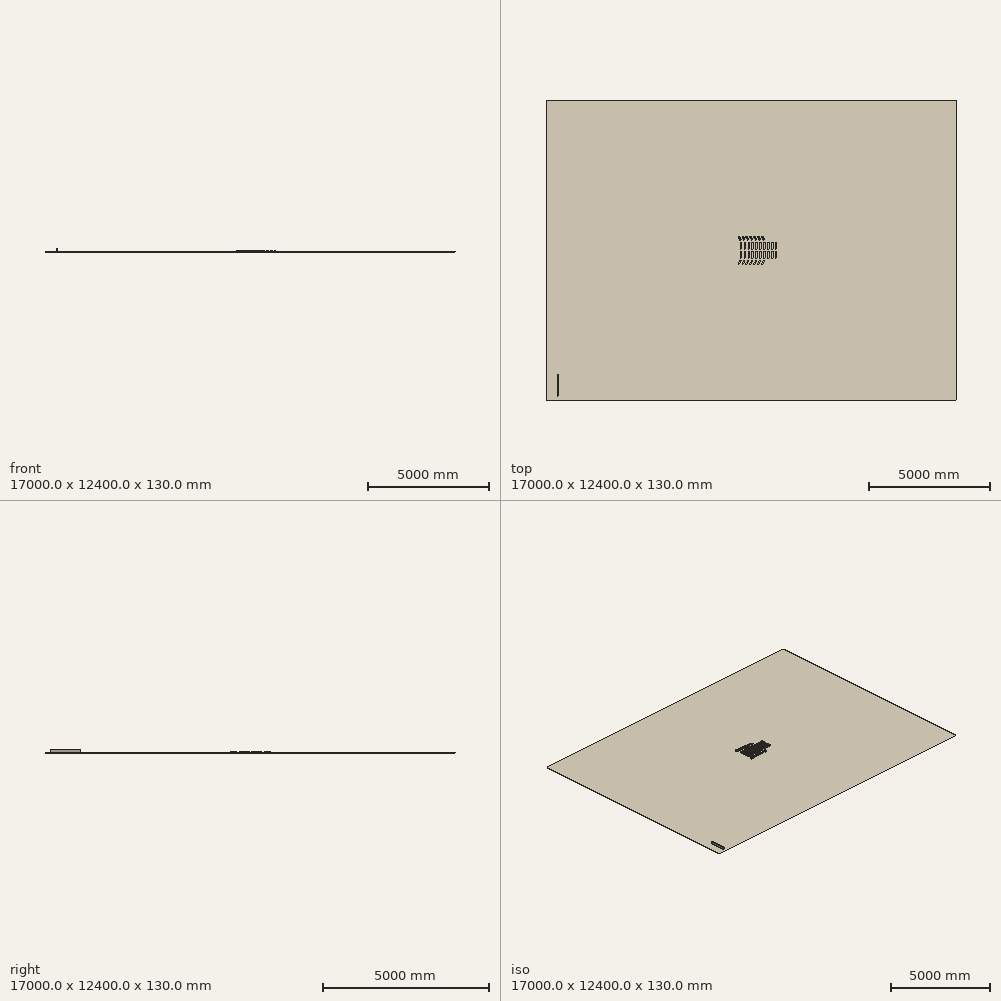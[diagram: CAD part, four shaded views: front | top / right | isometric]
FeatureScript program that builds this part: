
annotation { "Feature Type Name" : "Feature", "Feature Type Description" : "" }
export const myFeature = defineFeature(function(context is Context, id is Id, definition is map)
    precondition{}
    {
        {
            var Q0;
            Q0=qCreatedBy(makeId("Top.planeOp"),FACE);
            var sketch = newSketch(context, id + "F0", { "sketchPlane" : qUnion([Q0])});
            skLineSegment(sketch, "E0.bottom", {"start": v(8500, -6200) * mm, "end": v(-8500, -6200) * mm});
            skLineSegment(sketch, "E0.top", {"start": v(8500, 6200) * mm, "end": v(-8500, 6200) * mm});
            skLineSegment(sketch, "E0.left", {"start": v(8500, -6200) * mm, "end": v(8500, 6200) * mm});
            skLineSegment(sketch, "E0.right", {"start": v(-8500, -6200) * mm, "end": v(-8500, 6200) * mm});
            skPoint(sketch, "E0.middle", {"position": v(0, 0) * mm});
            skSolve(sketch);
        }
        {
            var Q0;
            Q0 = qSketchRegion(id + "F0", true);
            extrude(context, id + "F1", {"entities" : qUnion([Q0]), "depth" : 20 * mm});
        }
        {
            var Q0;
            Q0=qCreatedBy(makeId("Top.planeOp"),FACE);
            var sketch = newSketch(context, id + "F2", { "sketchPlane" : qUnion([Q0])});
            skLineSegment(sketch, "E1.bottom", {"start": v(-8040, -5150) * mm, "end": v(-8000, -5150) * mm});
            skLineSegment(sketch, "E1.top", {"start": v(-8040, -6050) * mm, "end": v(-8000, -6050) * mm});
            skLineSegment(sketch, "E1.left", {"start": v(-8040, -5150) * mm, "end": v(-8040, -6050) * mm});
            skLineSegment(sketch, "E1.right", {"start": v(-8000, -5150) * mm, "end": v(-8000, -6050) * mm});
            skSolve(sketch);
        }
        {
            var Q0;
            Q0 = qSketchRegion(id + "F2", true);
            extrude(context, id + "F3", {"entities" : qUnion([Q0]), "depth" : 130 * mm});
        }
        {
            var Q0;
            Q0=makeQuery(id+"F1.opExtrude","CAP_FACE",FACE,{"disambiguationData":[OSD([sQuery(id+"F0.wireOp",EDGE,"E0.bottom"),sQuery(id+"F0.wireOp",EDGE,"E0.top"),sQuery(id+"F0.wireOp",EDGE,"E0.left"),sQuery(id+"F0.wireOp",EDGE,"E0.right")])],"isStart":false});
            var sketch = newSketch(context, id + "F4", { "sketchPlane" : qUnion([Q0])});
            skLineSegment(sketch, "E2", {"start": v(-518.43, 595) * mm, "end": v(-428.43, 439.12) * mm});
            skLineSegment(sketch, "E3.0", {"start": v(-561.73, 570) * mm, "end": v(-471.73, 414.12) * mm});
            skLineSegment(sketch, "E4", {"start": v(-561.73, 570) * mm, "end": v(-518.43, 595) * mm});
            skLineSegment(sketch, "E5", {"start": v(-471.73, 414.12) * mm, "end": v(-428.43, 439.12) * mm});
            skLineSegment(sketch, "E6.1.0.0", {"start": v(-398.41, 570) * mm, "end": v(-308.41, 414.12) * mm});
            skLineSegment(sketch, "E6.1.0.1", {"start": v(-308.41, 414.12) * mm, "end": v(-265.11, 439.12) * mm});
            skLineSegment(sketch, "E6.1.0.2", {"start": v(-355.11, 595) * mm, "end": v(-265.11, 439.12) * mm});
            skLineSegment(sketch, "E6.1.0.3", {"start": v(-398.41, 570) * mm, "end": v(-355.11, 595) * mm});
            skLineSegment(sketch, "E6.2.0.0", {"start": v(-235.1, 570) * mm, "end": v(-145.1, 414.12) * mm});
            skLineSegment(sketch, "E6.2.0.1", {"start": v(-145.1, 414.12) * mm, "end": v(-101.8, 439.12) * mm});
            skLineSegment(sketch, "E6.2.0.2", {"start": v(-191.8, 595) * mm, "end": v(-101.8, 439.12) * mm});
            skLineSegment(sketch, "E6.2.0.3", {"start": v(-235.1, 570) * mm, "end": v(-191.8, 595) * mm});
            skLineSegment(sketch, "E6.3.0.0", {"start": v(-71.78, 570) * mm, "end": v(18.22, 414.12) * mm});
            skLineSegment(sketch, "E6.3.0.1", {"start": v(18.22, 414.12) * mm, "end": v(61.53, 439.12) * mm});
            skLineSegment(sketch, "E6.3.0.2", {"start": v(-28.47, 595) * mm, "end": v(61.53, 439.12) * mm});
            skLineSegment(sketch, "E6.3.0.3", {"start": v(-71.78, 570) * mm, "end": v(-28.47, 595) * mm});
            skLineSegment(sketch, "E6.4.0.0", {"start": v(91.54, 570) * mm, "end": v(181.54, 414.12) * mm});
            skLineSegment(sketch, "E6.4.0.1", {"start": v(181.54, 414.12) * mm, "end": v(224.85, 439.12) * mm});
            skLineSegment(sketch, "E6.4.0.2", {"start": v(134.85, 595) * mm, "end": v(224.85, 439.12) * mm});
            skLineSegment(sketch, "E6.4.0.3", {"start": v(91.54, 570) * mm, "end": v(134.85, 595) * mm});
            skLineSegment(sketch, "E6.5.0.0", {"start": v(254.86, 570) * mm, "end": v(344.86, 414.12) * mm});
            skLineSegment(sketch, "E6.5.0.1", {"start": v(344.86, 414.12) * mm, "end": v(388.16, 439.12) * mm});
            skLineSegment(sketch, "E6.5.0.2", {"start": v(298.16, 595) * mm, "end": v(388.16, 439.12) * mm});
            skLineSegment(sketch, "E6.5.0.3", {"start": v(254.86, 570) * mm, "end": v(298.16, 595) * mm});
            skLineSegment(sketch, "E6.6.0.0", {"start": v(418.18, 570) * mm, "end": v(508.18, 414.12) * mm});
            skLineSegment(sketch, "E6.6.0.1", {"start": v(508.18, 414.12) * mm, "end": v(551.48, 439.12) * mm});
            skLineSegment(sketch, "E6.6.0.2", {"start": v(461.48, 595) * mm, "end": v(551.48, 439.12) * mm});
            skLineSegment(sketch, "E6.6.0.3", {"start": v(418.18, 570) * mm, "end": v(461.48, 595) * mm});
            skLineSegment(sketch, "E6.direction1", {"start": v(-561.73, 570) * mm, "end": v(-398.41, 570) * mm, "construction": true});
            skLineSegment(sketch, "E7", {"start": v(-8500, 0) * mm, "end": v(8500, 0) * mm, "construction": true});
            skLineSegment(sketch, "E8.bottom", {"start": v(-469.55, 30) * mm, "end": v(-409.55, 30) * mm});
            skLineSegment(sketch, "E8.top", {"start": v(-469.55, 328.32) * mm, "end": v(-409.55, 328.32) * mm});
            skLineSegment(sketch, "E8.left", {"start": v(-469.55, 30) * mm, "end": v(-469.55, 328.32) * mm});
            skLineSegment(sketch, "E8.right", {"start": v(-409.55, 30) * mm, "end": v(-409.55, 328.32) * mm});
            skLineSegment(sketch, "E9.1.0.0", {"start": v(-306.63, 30) * mm, "end": v(-246.63, 30) * mm});
            skLineSegment(sketch, "E9.1.0.1", {"start": v(-306.63, 30) * mm, "end": v(-306.63, 328.32) * mm});
            skLineSegment(sketch, "E9.1.0.2", {"start": v(-306.63, 328.32) * mm, "end": v(-246.63, 328.32) * mm});
            skLineSegment(sketch, "E9.1.0.3", {"start": v(-246.63, 30) * mm, "end": v(-246.63, 328.32) * mm});
            skLineSegment(sketch, "E9.2.0.0", {"start": v(-143.71, 30) * mm, "end": v(-83.71, 30) * mm});
            skLineSegment(sketch, "E9.2.0.1", {"start": v(-143.71, 30) * mm, "end": v(-143.71, 328.32) * mm});
            skLineSegment(sketch, "E9.2.0.2", {"start": v(-143.71, 328.32) * mm, "end": v(-83.71, 328.32) * mm});
            skLineSegment(sketch, "E9.2.0.3", {"start": v(-83.71, 30) * mm, "end": v(-83.71, 328.32) * mm});
            skLineSegment(sketch, "E9.3.0.0", {"start": v(19.2, 30) * mm, "end": v(79.2, 30) * mm});
            skLineSegment(sketch, "E9.3.0.1", {"start": v(19.2, 30) * mm, "end": v(19.2, 328.32) * mm});
            skLineSegment(sketch, "E9.3.0.2", {"start": v(19.2, 328.32) * mm, "end": v(79.2, 328.32) * mm});
            skLineSegment(sketch, "E9.3.0.3", {"start": v(79.2, 30) * mm, "end": v(79.2, 328.32) * mm});
            skLineSegment(sketch, "E9.4.0.0", {"start": v(182.13, 30) * mm, "end": v(242.13, 30) * mm});
            skLineSegment(sketch, "E9.4.0.1", {"start": v(182.13, 30) * mm, "end": v(182.13, 328.32) * mm});
            skLineSegment(sketch, "E9.4.0.2", {"start": v(182.13, 328.32) * mm, "end": v(242.13, 328.32) * mm});
            skLineSegment(sketch, "E9.4.0.3", {"start": v(242.13, 30) * mm, "end": v(242.13, 328.32) * mm});
            skLineSegment(sketch, "E9.5.0.0", {"start": v(345.04, 30) * mm, "end": v(405.04, 30) * mm});
            skLineSegment(sketch, "E9.5.0.1", {"start": v(345.04, 30) * mm, "end": v(345.04, 328.32) * mm});
            skLineSegment(sketch, "E9.5.0.2", {"start": v(345.04, 328.32) * mm, "end": v(405.04, 328.32) * mm});
            skLineSegment(sketch, "E9.5.0.3", {"start": v(405.04, 30) * mm, "end": v(405.04, 328.32) * mm});
            skLineSegment(sketch, "E9.6.0.0", {"start": v(507.96, 30) * mm, "end": v(567.96, 30) * mm});
            skLineSegment(sketch, "E9.6.0.1", {"start": v(507.96, 30) * mm, "end": v(507.96, 328.32) * mm});
            skLineSegment(sketch, "E9.6.0.2", {"start": v(507.96, 328.32) * mm, "end": v(567.96, 328.32) * mm});
            skLineSegment(sketch, "E9.6.0.3", {"start": v(567.96, 30) * mm, "end": v(567.96, 328.32) * mm});
            skLineSegment(sketch, "E9.7.0.0", {"start": v(670.88, 30) * mm, "end": v(730.88, 30) * mm});
            skLineSegment(sketch, "E9.7.0.1", {"start": v(670.88, 30) * mm, "end": v(670.88, 328.32) * mm});
            skLineSegment(sketch, "E9.7.0.2", {"start": v(670.88, 328.32) * mm, "end": v(730.88, 328.32) * mm});
            skLineSegment(sketch, "E9.7.0.3", {"start": v(730.88, 30) * mm, "end": v(730.88, 328.32) * mm});
            skLineSegment(sketch, "E9.8.0.0", {"start": v(833.8, 30) * mm, "end": v(893.8, 30) * mm});
            skLineSegment(sketch, "E9.8.0.1", {"start": v(833.8, 30) * mm, "end": v(833.8, 328.32) * mm});
            skLineSegment(sketch, "E9.8.0.2", {"start": v(833.8, 328.32) * mm, "end": v(893.8, 328.32) * mm});
            skLineSegment(sketch, "E9.8.0.3", {"start": v(893.8, 30) * mm, "end": v(893.8, 328.32) * mm});
            skLineSegment(sketch, "E9.9.0.0", {"start": v(996.71, 30) * mm, "end": v(1056.71, 30) * mm});
            skLineSegment(sketch, "E9.9.0.1", {"start": v(996.71, 30) * mm, "end": v(996.71, 328.32) * mm});
            skLineSegment(sketch, "E9.9.0.2", {"start": v(996.71, 328.32) * mm, "end": v(1056.71, 328.32) * mm});
            skLineSegment(sketch, "E9.9.0.3", {"start": v(1056.71, 30) * mm, "end": v(1056.71, 328.32) * mm});
            skLineSegment(sketch, "E9.direction1", {"start": v(-409.55, 30) * mm, "end": v(-246.63, 30) * mm, "construction": true});
            skLineSegment(sketch, "E10", {"start": v(-8500, -30) * mm, "end": v(-8500, 0) * mm, "construction": true});
            skLineSegment(sketch, "E11.MirrorCS", {"start": v(8500, -30) * mm, "end": v(8500, 0) * mm, "construction": true});
            skLineSegment(sketch, "E12", {"start": v(8500, 6200) * mm, "end": v(8500, -6200) * mm});
            skLineSegment(sketch, "E13.MirrorCS", {"start": v(-561.73, -570) * mm, "end": v(-471.73, -414.12) * mm});
            skLineSegment(sketch, "E14.MirrorCS", {"start": v(-398.41, -570) * mm, "end": v(-308.41, -414.12) * mm});
            skLineSegment(sketch, "E15.MirrorCS", {"start": v(-471.73, -414.12) * mm, "end": v(-428.43, -439.12) * mm});
            skLineSegment(sketch, "E16.MirrorCS", {"start": v(-561.73, -570) * mm, "end": v(-518.43, -595) * mm});
            skLineSegment(sketch, "E17.MirrorCS", {"start": v(-518.43, -595) * mm, "end": v(-428.43, -439.12) * mm});
            skLineSegment(sketch, "E18.MirrorCS", {"start": v(134.85, -595) * mm, "end": v(224.85, -439.12) * mm});
            skLineSegment(sketch, "E19.MirrorCS", {"start": v(1056.71, -30) * mm, "end": v(1056.71, -328.32) * mm});
            skLineSegment(sketch, "E20.MirrorCS", {"start": v(-306.63, -30) * mm, "end": v(-246.63, -30) * mm});
            skLineSegment(sketch, "E21.MirrorCS", {"start": v(-469.55, -328.32) * mm, "end": v(-409.55, -328.32) * mm});
            skLineSegment(sketch, "E22.MirrorCS", {"start": v(345.04, -30) * mm, "end": v(405.04, -30) * mm});
            skLineSegment(sketch, "E23.MirrorCS", {"start": v(418.18, -570) * mm, "end": v(461.48, -595) * mm});
            skLineSegment(sketch, "E24.MirrorCS", {"start": v(182.13, -30) * mm, "end": v(182.13, -328.32) * mm});
            skLineSegment(sketch, "E25.MirrorCS", {"start": v(996.71, -30) * mm, "end": v(1056.71, -30) * mm});
            skLineSegment(sketch, "E26.MirrorCS", {"start": v(-308.41, -414.12) * mm, "end": v(-265.11, -439.12) * mm});
            skLineSegment(sketch, "E27.MirrorCS", {"start": v(19.2, -30) * mm, "end": v(19.2, -328.32) * mm});
            skLineSegment(sketch, "E28.MirrorCS", {"start": v(833.8, -30) * mm, "end": v(833.8, -328.32) * mm});
            skLineSegment(sketch, "E29.MirrorCS", {"start": v(670.88, -30) * mm, "end": v(670.88, -328.32) * mm});
            skLineSegment(sketch, "E30.MirrorCS", {"start": v(418.18, -570) * mm, "end": v(508.18, -414.12) * mm});
            skLineSegment(sketch, "E31.MirrorCS", {"start": v(-355.11, -595) * mm, "end": v(-265.11, -439.12) * mm});
            skLineSegment(sketch, "E32.MirrorCS", {"start": v(254.86, -570) * mm, "end": v(344.86, -414.12) * mm});
            skLineSegment(sketch, "E33.MirrorCS", {"start": v(-143.71, -328.32) * mm, "end": v(-83.71, -328.32) * mm});
            skLineSegment(sketch, "E34.MirrorCS", {"start": v(18.22, -414.12) * mm, "end": v(61.53, -439.12) * mm});
            skLineSegment(sketch, "E35.MirrorCS", {"start": v(-306.63, -328.32) * mm, "end": v(-246.63, -328.32) * mm});
            skLineSegment(sketch, "E36.MirrorCS", {"start": v(507.96, -328.32) * mm, "end": v(567.96, -328.32) * mm});
            skLineSegment(sketch, "E37.MirrorCS", {"start": v(345.04, -328.32) * mm, "end": v(405.04, -328.32) * mm});
            skLineSegment(sketch, "E38.MirrorCS", {"start": v(181.54, -414.12) * mm, "end": v(224.85, -439.12) * mm});
            skLineSegment(sketch, "E39.MirrorCS", {"start": v(-28.47, -595) * mm, "end": v(61.53, -439.12) * mm});
            skLineSegment(sketch, "E40.MirrorCS", {"start": v(996.71, -328.32) * mm, "end": v(1056.71, -328.32) * mm});
            skLineSegment(sketch, "E41.MirrorCS", {"start": v(-409.55, -30) * mm, "end": v(-409.55, -328.32) * mm});
            skLineSegment(sketch, "E42.MirrorCS", {"start": v(-469.55, -30) * mm, "end": v(-409.55, -30) * mm});
            skLineSegment(sketch, "E43.MirrorCS", {"start": v(242.13, -30) * mm, "end": v(242.13, -328.32) * mm});
            skLineSegment(sketch, "E44.MirrorCS", {"start": v(-71.78, -570) * mm, "end": v(-28.47, -595) * mm});
            skLineSegment(sketch, "E45.MirrorCS", {"start": v(461.48, -595) * mm, "end": v(551.48, -439.12) * mm});
            skLineSegment(sketch, "E46.MirrorCS", {"start": v(-398.41, -570) * mm, "end": v(-355.11, -595) * mm});
            skLineSegment(sketch, "E47.MirrorCS", {"start": v(182.13, -30) * mm, "end": v(242.13, -30) * mm});
            skLineSegment(sketch, "E48.MirrorCS", {"start": v(893.8, -30) * mm, "end": v(893.8, -328.32) * mm});
            skLineSegment(sketch, "E49.MirrorCS", {"start": v(298.16, -595) * mm, "end": v(388.16, -439.12) * mm});
            skLineSegment(sketch, "E50.MirrorCS", {"start": v(19.2, -30) * mm, "end": v(79.2, -30) * mm});
            skLineSegment(sketch, "E51.MirrorCS", {"start": v(833.8, -30) * mm, "end": v(893.8, -30) * mm});
            skLineSegment(sketch, "E52.MirrorCS", {"start": v(-143.71, -30) * mm, "end": v(-83.71, -30) * mm});
            skLineSegment(sketch, "E53.MirrorCS", {"start": v(670.88, -30) * mm, "end": v(730.88, -30) * mm});
            skLineSegment(sketch, "E54.MirrorCS", {"start": v(-235.1, -570) * mm, "end": v(-145.1, -414.12) * mm});
            skLineSegment(sketch, "E55.MirrorCS", {"start": v(254.86, -570) * mm, "end": v(298.16, -595) * mm});
            skLineSegment(sketch, "E56.MirrorCS", {"start": v(507.96, -30) * mm, "end": v(567.96, -30) * mm});
            skLineSegment(sketch, "E57.MirrorCS", {"start": v(91.54, -570) * mm, "end": v(134.85, -595) * mm});
            skLineSegment(sketch, "E58.MirrorCS", {"start": v(-143.71, -30) * mm, "end": v(-143.71, -328.32) * mm});
            skLineSegment(sketch, "E59.MirrorCS", {"start": v(-409.55, -30) * mm, "end": v(-246.63, -30) * mm, "construction": true});
            skLineSegment(sketch, "E60.MirrorCS", {"start": v(-145.1, -414.12) * mm, "end": v(-101.8, -439.12) * mm});
            skLineSegment(sketch, "E61.MirrorCS", {"start": v(-306.63, -30) * mm, "end": v(-306.63, -328.32) * mm});
            skLineSegment(sketch, "E62.MirrorCS", {"start": v(507.96, -30) * mm, "end": v(507.96, -328.32) * mm});
            skLineSegment(sketch, "E63.MirrorCS", {"start": v(345.04, -30) * mm, "end": v(345.04, -328.32) * mm});
            skLineSegment(sketch, "E64.MirrorCS", {"start": v(-561.73, -570) * mm, "end": v(-398.41, -570) * mm, "construction": true});
            skLineSegment(sketch, "E65.MirrorCS", {"start": v(91.54, -570) * mm, "end": v(181.54, -414.12) * mm});
            skLineSegment(sketch, "E66.MirrorCS", {"start": v(-191.8, -595) * mm, "end": v(-101.8, -439.12) * mm});
            skLineSegment(sketch, "E67.MirrorCS", {"start": v(996.71, -30) * mm, "end": v(996.71, -328.32) * mm});
            skLineSegment(sketch, "E68.MirrorCS", {"start": v(19.2, -328.32) * mm, "end": v(79.2, -328.32) * mm});
            skLineSegment(sketch, "E69.MirrorCS", {"start": v(-469.55, -30) * mm, "end": v(-469.55, -328.32) * mm});
            skLineSegment(sketch, "E70.MirrorCS", {"start": v(670.88, -328.32) * mm, "end": v(730.88, -328.32) * mm});
            skLineSegment(sketch, "E71.MirrorCS", {"start": v(182.13, -328.32) * mm, "end": v(242.13, -328.32) * mm});
            skLineSegment(sketch, "E72.MirrorCS", {"start": v(508.18, -414.12) * mm, "end": v(551.48, -439.12) * mm});
            skLineSegment(sketch, "E73.MirrorCS", {"start": v(-235.1, -570) * mm, "end": v(-191.8, -595) * mm});
            skLineSegment(sketch, "E74.MirrorCS", {"start": v(79.2, -30) * mm, "end": v(79.2, -328.32) * mm});
            skLineSegment(sketch, "E75.MirrorCS", {"start": v(833.8, -328.32) * mm, "end": v(893.8, -328.32) * mm});
            skLineSegment(sketch, "E76.MirrorCS", {"start": v(344.86, -414.12) * mm, "end": v(388.16, -439.12) * mm});
            skLineSegment(sketch, "E77.MirrorCS", {"start": v(-83.71, -30) * mm, "end": v(-83.71, -328.32) * mm});
            skLineSegment(sketch, "E78.MirrorCS", {"start": v(730.88, -30) * mm, "end": v(730.88, -328.32) * mm});
            skLineSegment(sketch, "E79.MirrorCS", {"start": v(-246.63, -30) * mm, "end": v(-246.63, -328.32) * mm});
            skLineSegment(sketch, "E80.MirrorCS", {"start": v(567.96, -30) * mm, "end": v(567.96, -328.32) * mm});
            skLineSegment(sketch, "E81.MirrorCS", {"start": v(-71.78, -570) * mm, "end": v(18.22, -414.12) * mm});
            skLineSegment(sketch, "E82.MirrorCS", {"start": v(405.04, -30) * mm, "end": v(405.04, -328.32) * mm});
            skSolve(sketch);
        }
        {
            var Q0;
            Q0 = qSketchRegion(id + "F4", true);
            extrude(context, id + "F5", {"entities" : qUnion([Q0]), "depth" : 50 * mm});
        }
    });
